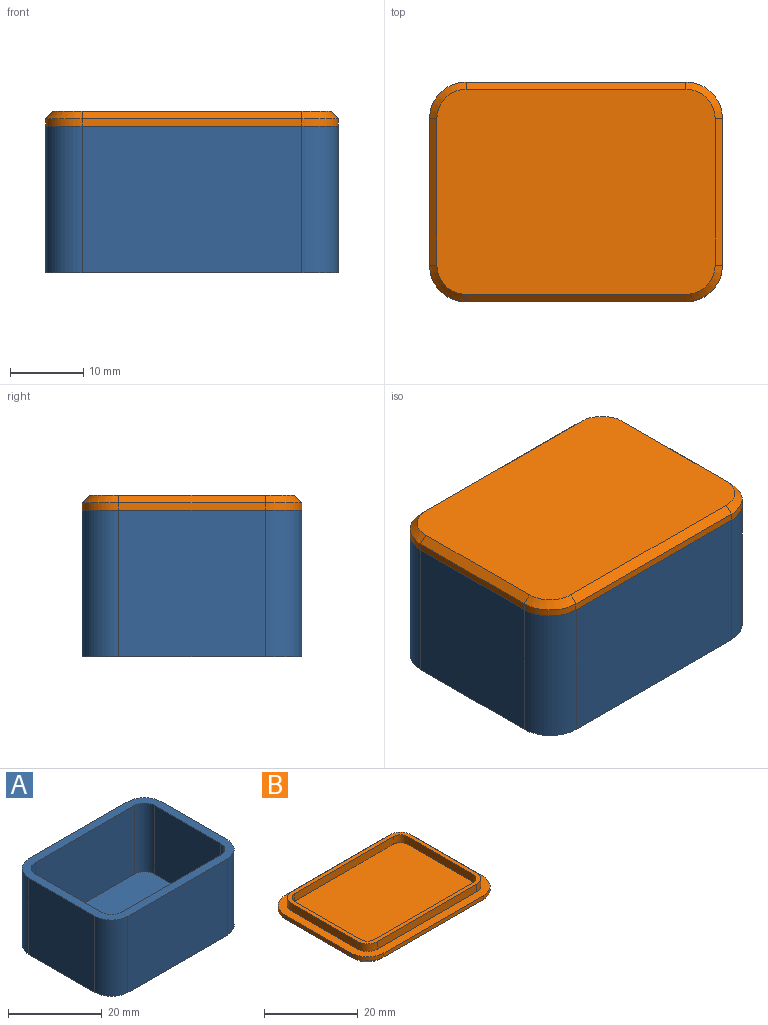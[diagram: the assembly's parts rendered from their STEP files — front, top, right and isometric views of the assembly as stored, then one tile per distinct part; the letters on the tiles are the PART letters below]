
ASSEMBLY  parts=2 mates=1
PART A: 19 faces, bbox 40x30x20 mm
  f0: plane 40x30mm, normal (0,0,1), area 250.3mm2, adj f1,f2,f3,f4,f5,f6,f7,f8
  f1: plane 20x20mm, normal (1,0,0), area 400mm2, adj f0,f2,f8,f9
  f2: cylinder r=5mm len=20mm, axis (0,0,-1), area 157.1mm2, adj f0,f1,f3,f9
  f3: plane 30x20mm, normal (0,1,0), area 600mm2, adj f0,f2,f4,f9
  f4: cylinder r=5mm len=20mm, axis (0,0,-1), area 157.1mm2, adj f0,f3,f5,f9
  f5: plane 20x20mm, normal (-1,0,0), area 400mm2, adj f0,f4,f6,f9
  f6: cylinder r=5mm len=20mm, axis (0,0,-1), area 157.1mm2, adj f0,f5,f7,f9
  f7: plane 30x20mm, normal (0,-1,0), area 600mm2, adj f0,f6,f8,f9
  f8: cylinder r=5mm len=20mm, axis (0,0,-1), area 157.1mm2, adj f0,f1,f7,f9
  f9: plane 40x30mm, normal (0,0,-1), area 1178.5mm2, adj f1,f2,f3,f4,f5,f6,f7,f8
  f10: plane 20x18mm, normal (-1,0,0), area 360mm2, adj f0,f11,f17,f18
  f11: cylinder r=3mm len=18mm, axis (0,0,-1), area 84.8mm2, adj f0,f10,f12,f18
  f12: plane 30x18mm, normal (0,-1,0), area 540mm2, adj f0,f11,f13,f18
  f13: cylinder r=3mm len=18mm, axis (0,0,-1), area 84.8mm2, adj f0,f12,f14,f18
  f14: plane 20x18mm, normal (1,0,0), area 360mm2, adj f0,f13,f15,f18
  f15: cylinder r=3mm len=18mm, axis (0,0,-1), area 84.8mm2, adj f0,f14,f16,f18
  f16: plane 30x18mm, normal (0,1,0), area 540mm2, adj f0,f15,f17,f18
  f17: cylinder r=3mm len=18mm, axis (0,0,-1), area 84.8mm2, adj f0,f10,f16,f18
  f18: plane 36x26mm, normal (0,0,1), area 928.3mm2, adj f10,f11,f12,f13,f14,f15,f16,f17
PART B: 36 faces, bbox 40x30x4 mm
  f0: plane 40x30mm, normal (0,0,1), area 250.3mm2, adj f1,f2,f3,f4,f5,f6,f7,f8
  f1: plane 20x1mm, normal (1,0,0), area 20mm2, adj f0,f2,f8,f31
  f2: cylinder r=5mm len=5mm, axis (0,0,-1), area 7.9mm2, adj f0,f1,f3,f33
  f3: plane 30x1mm, normal (0,1,0), area 30mm2, adj f0,f2,f4,f35
  f4: cylinder r=5mm len=5mm, axis (0,0,-1), area 7.9mm2, adj f0,f3,f5,f34
  f5: plane 20x1mm, normal (-1,0,0), area 20mm2, adj f0,f4,f6,f32
  f6: cylinder r=5mm len=5mm, axis (0,0,-1), area 7.9mm2, adj f0,f5,f7,f30
  f7: plane 30x1mm, normal (0,-1,0), area 30mm2, adj f0,f6,f8,f28
  f8: cylinder r=5mm len=5mm, axis (0,0,-1), area 7.9mm2, adj f0,f1,f7,f29
  f9: plane 38x28mm, normal (0,0,-1), area 1050.3mm2, adj f28,f29,f30,f31,f32,f33,f34,f35
  f10: plane 30x2mm, normal (0,-1,0), area 60mm2, adj f11,f25,f26,f27
  f11: cylinder r=2mm len=2mm, axis (0,0,-1), area 6.3mm2, adj f10,f12,f26,f27
  f12: plane 20x2mm, normal (-1,0,0), area 40mm2, adj f11,f13,f26,f27
  f13: cylinder r=2mm len=2mm, axis (0,0,-1), area 6.3mm2, adj f12,f14,f26,f27
  f14: plane 30x2mm, normal (0,1,0), area 60mm2, adj f13,f15,f26,f27
  f15: cylinder r=2mm len=2mm, axis (0,0,-1), area 6.3mm2, adj f14,f16,f26,f27
  f16: plane 20x2mm, normal (1,0,0), area 40mm2, adj f15,f25,f26,f27
  f17: plane 20x2mm, normal (1,0,0), area 40mm2, adj f0,f18,f24,f26
  f18: cylinder r=3mm len=3mm, axis (0,0,-1), area 9.4mm2, adj f0,f17,f19,f26
  f19: plane 30x2mm, normal (0,1,0), area 60mm2, adj f0,f18,f20,f26
  f20: cylinder r=3mm len=3mm, axis (0,0,-1), area 9.4mm2, adj f0,f19,f21,f26
  f21: plane 20x2mm, normal (-1,0,0), area 40mm2, adj f0,f20,f22,f26
  f22: cylinder r=3mm len=3mm, axis (0,0,-1), area 9.4mm2, adj f0,f21,f23,f26
  f23: plane 30x2mm, normal (0,-1,0), area 60mm2, adj f0,f22,f24,f26
  f24: cylinder r=3mm len=3mm, axis (0,0,-1), area 9.4mm2, adj f0,f17,f23,f26
  f25: cylinder r=2mm len=2mm, axis (0,0,-1), area 6.3mm2, adj f10,f16,f26,f27
  f26: plane 36x26mm, normal (0,0,1), area 115.7mm2, adj f10,f11,f12,f13,f14,f15,f16,f17
  f27: plane 34x24mm, normal (0,0,1), area 812.6mm2, adj f10,f11,f12,f13,f14,f15,f16,f25
  f28: plane 30x1mm, normal (0,-0.71,-0.71), area 42.4mm2, adj f7,f9,f29,f30
  f29: cone r=5mm half-angle=45deg, axis (0,0,1), area 10mm2, adj f8,f9,f28,f31
  f30: cone r=5mm half-angle=45deg, axis (0,0,1), area 10mm2, adj f6,f9,f28,f32
  f31: plane 20x1mm, normal (0.71,0,-0.71), area 28.3mm2, adj f1,f9,f29,f33
  f32: plane 20x1mm, normal (-0.71,0,-0.71), area 28.3mm2, adj f5,f9,f30,f34
  f33: cone r=5mm half-angle=45deg, axis (0,0,1), area 10mm2, adj f2,f9,f31,f35
  f34: cone r=5mm half-angle=45deg, axis (0,0,1), area 10mm2, adj f4,f9,f32,f35
  f35: plane 30x1mm, normal (0,0.71,-0.71), area 42.4mm2, adj f3,f9,f33,f34
PLACE A at identity
PLACE B rot(axis=(1,0,0),180deg) t=(0,0,22)mm
MATE fastened B.f8 <-> A.f2  axis (0,0,-1) through (15,10,20)mm
